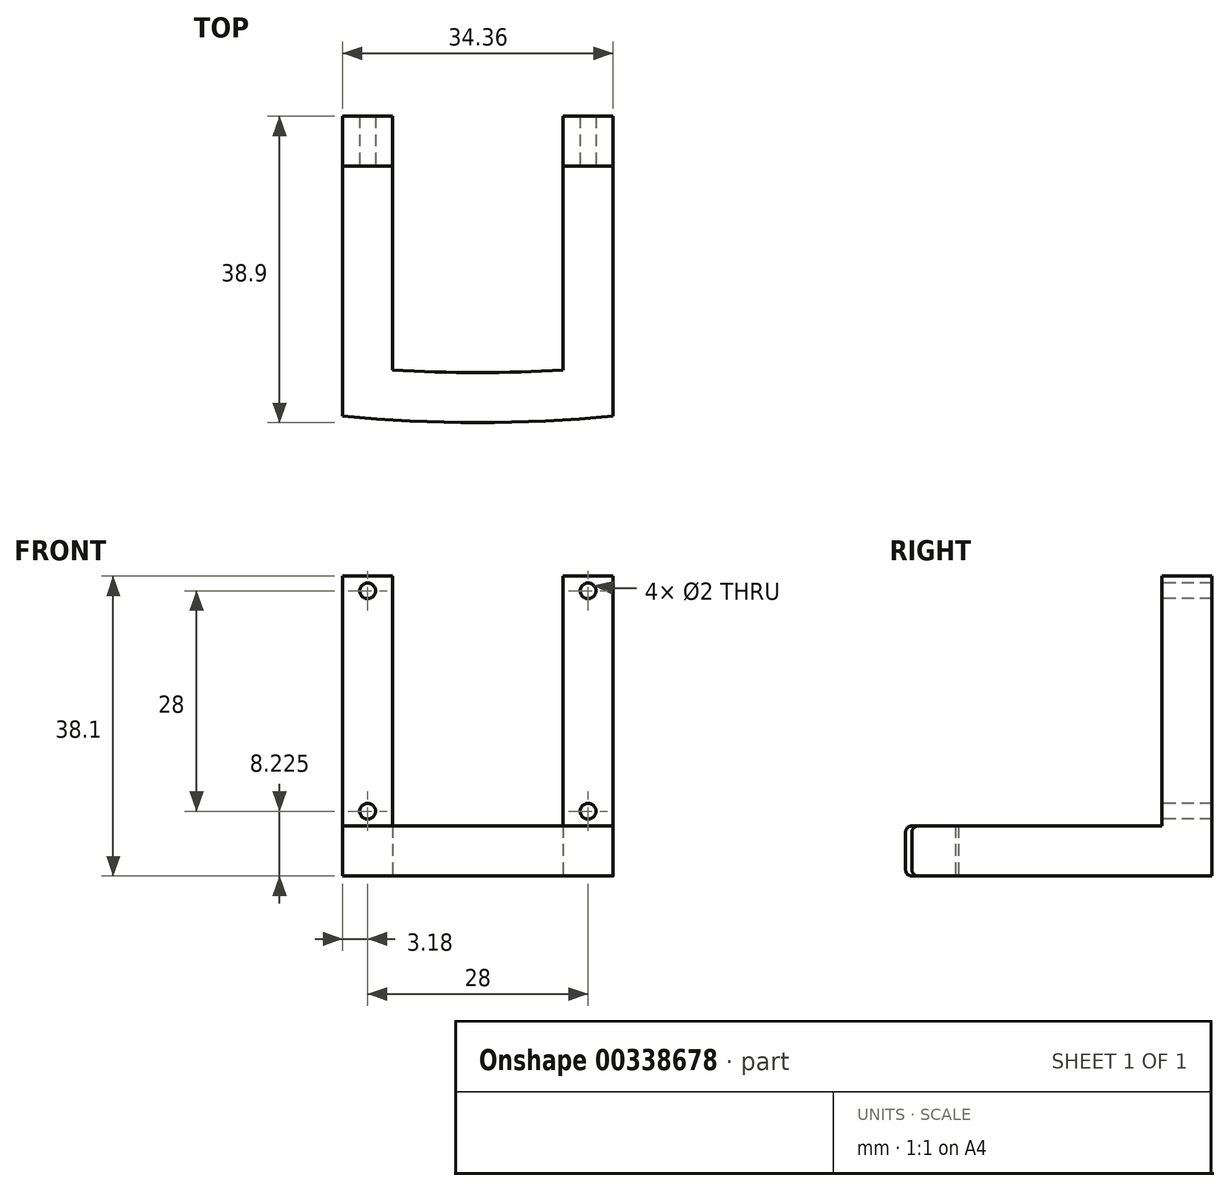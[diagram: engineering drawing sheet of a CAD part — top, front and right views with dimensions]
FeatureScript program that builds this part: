
annotation { "Feature Type Name" : "Feature", "Feature Type Description" : "" }
export const myFeature = defineFeature(function(context is Context, id is Id, definition is map)
    precondition{}
    {
        {
            var Q0;
            Q0=qCreatedBy(makeId("Top.planeOp"),FACE);
            var sketch = newSketch(context, id + "F0", { "sketchPlane" : qUnion([Q0])});
            skLineSegment(sketch, "E0.bottom", {"start": v(-10.82, 0) * mm, "end": v(-17.18, 0) * mm});
            skLineSegment(sketch, "E0.top", {"start": v(-10.82, 38.1) * mm, "end": v(-17.17, 38.1) * mm});
            skLineSegment(sketch, "E0.left", {"start": v(-10.82, 0) * mm, "end": v(-10.82, 38.1) * mm});
            skLineSegment(sketch, "E0.right", {"start": v(-17.18, 0) * mm, "end": v(-17.17, 38.1) * mm});
            skLineSegment(sketch, "E1.bottom", {"start": v(10.82, 0) * mm, "end": v(17.18, 0) * mm});
            skLineSegment(sketch, "E1.top", {"start": v(10.82, 38.1) * mm, "end": v(17.17, 38.1) * mm});
            skLineSegment(sketch, "E1.left", {"start": v(10.82, 0) * mm, "end": v(10.82, 38.1) * mm});
            skLineSegment(sketch, "E1.right", {"start": v(17.18, 0) * mm, "end": v(17.17, 38.1) * mm});
            skArc(sketch, "E2", {"start": v(-17.18, 0) * mm, "mid": v(0, -0.8) * mm, "end": v(17.17, 0) * mm});
            skArc(sketch, "E3", {"start": v(-10.83, 5.88) * mm, "mid": v(0, 5.55) * mm, "end": v(10.82, 5.88) * mm});
            skLineSegment(sketch, "E4.bottom", {"start": v(-17.17, 38.1) * mm, "end": v(-10.82, 38.1) * mm});
            skLineSegment(sketch, "E4.top", {"start": v(-17.17, 31.76) * mm, "end": v(-10.82, 31.76) * mm});
            skLineSegment(sketch, "E4.left", {"start": v(-17.17, 38.1) * mm, "end": v(-17.17, 31.76) * mm});
            skLineSegment(sketch, "E4.right", {"start": v(-10.82, 38.1) * mm, "end": v(-10.82, 31.76) * mm});
            skLineSegment(sketch, "E5.MirrorCS", {"start": v(10.82, 38.1) * mm, "end": v(10.82, 31.76) * mm});
            skLineSegment(sketch, "E6.MirrorCS", {"start": v(17.17, 38.1) * mm, "end": v(17.17, 31.76) * mm});
            skLineSegment(sketch, "E7.MirrorCS", {"start": v(17.17, 38.1) * mm, "end": v(10.82, 38.1) * mm});
            skLineSegment(sketch, "E8.MirrorCS", {"start": v(17.17, 31.76) * mm, "end": v(10.82, 31.76) * mm});
            skLineSegment(sketch, "E9", {"start": v(10.82, 31.76) * mm, "end": v(10.82, 5.88) * mm});
            skSolve(sketch);
        }
        {
            var Q0;
            Q0=qCreatedBy(makeId("Top.planeOp"),FACE);
            var sketch = newSketch(context, id + "F1", { "sketchPlane" : qUnion([Q0])});
            skLineSegment(sketch, "E10.bottom", {"start": v(-17.18, 38.1) * mm, "end": v(-10.82, 38.1) * mm});
            skLineSegment(sketch, "E10.top", {"start": v(-17.18, 31.75) * mm, "end": v(-10.82, 31.75) * mm});
            skLineSegment(sketch, "E10.left", {"start": v(-17.18, 38.1) * mm, "end": v(-17.18, 31.75) * mm});
            skLineSegment(sketch, "E10.right", {"start": v(-10.82, 38.1) * mm, "end": v(-10.82, 31.75) * mm});
            skLineSegment(sketch, "E11.bottom", {"start": v(10.82, 38.1) * mm, "end": v(17.18, 38.1) * mm});
            skLineSegment(sketch, "E11.top", {"start": v(10.82, 31.75) * mm, "end": v(17.18, 31.75) * mm});
            skLineSegment(sketch, "E11.left", {"start": v(10.82, 38.1) * mm, "end": v(10.82, 31.75) * mm});
            skLineSegment(sketch, "E11.right", {"start": v(17.18, 38.1) * mm, "end": v(17.18, 31.75) * mm});
            skSolve(sketch);
        }
        {
            var Q0;
            Q0 = qSketchRegion(id + "F0", true);
            extrude(context, id + "F2", {"entities" : qUnion([Q0]), "depth" : 6.35 * mm});
        }
        {
            var Q0;
            Q0 = qSketchRegion(id + "F1", true);
            extrude(context, id + "F3", {"entities" : qUnion([Q0]), "operationType" : NewBodyOperationType.ADD, "depth" : 38.1 * mm});
        }
        {
            var Q0;
            Q0=makeQuery(id+"F3.opExtrude","SWEPT_FACE",FACE,{"disambiguationData":[OSD([sQuery(id+"F1.wireOp",EDGE,"E10.top")])]});
            var sketch = newSketch(context, id + "F4", { "sketchPlane" : qUnion([Q0])});
            skPoint(sketch, "E12", {"position": v(-14, 36.23) * mm});
            skPoint(sketch, "E12.positionSnap0", {"position": v(-14, 38.1) * mm});
            skPoint(sketch, "E13", {"position": v(-14, 8.22) * mm});
            skPoint(sketch, "E14.MirrorP", {"position": v(14, 36.23) * mm});
            skPoint(sketch, "E15.MirrorP", {"position": v(14, 8.22) * mm});
            skSolve(sketch);
        }
        {
            var Q0;
            Q0=sQuery(id+"F4.wireOp",VERTEX,"E12");
            var Q1;
            Q1=sQuery(id+"F4.wireOp",VERTEX,"E13");
            var Q2;
            Q2=sQuery(id+"F4.wireOp",VERTEX,"E15.MirrorP");
            var Q3;
            Q3=sQuery(id+"F4.wireOp",VERTEX,"E14.MirrorP");
            var Q4;
            Q4=makeQuery(id+"F2.opExtrude","SWEPT_BODY",BODY,{"disambiguationData":[OSD([sQuery(id+"F0.wireOp",EDGE,"E0.top"),sQuery(id+"F0.wireOp",EDGE,"E0.left"),sQuery(id+"F0.wireOp",EDGE,"E0.right"),sQuery(id+"F0.wireOp",EDGE,"E1.top"),sQuery(id+"F0.wireOp",EDGE,"E1.left"),sQuery(id+"F0.wireOp",EDGE,"E1.right"),sQuery(id+"F0.wireOp",EDGE,"E2"),sQuery(id+"F0.wireOp",EDGE,"E3")])]});
            hole(context, id + "F5", {"style" : HoleStyle.SIMPLE, "endStyle" : HoleEndStyle.THROUGH, "holeDiameter" : 2 * mm, "tappedDepth" : 12.7 * mm, "tapClearance" : 3, "locations" : qUnion([Q0, Q1, Q2, Q3]), "scope" : qUnion([Q4])});
        }
        {
            var Q0;
            Q0=makeQuery(id+"F2.opExtrude","CAP_EDGE",EDGE,{"disambiguationData":[OSD([sQuery(id+"F0.wireOp",EDGE,"E2")])],"isStart":false});
            var Q1;
            Q1=makeQuery(id+"F2.opExtrude","CAP_EDGE",EDGE,{"disambiguationData":[OSD([sQuery(id+"F0.wireOp",EDGE,"E2")])],"isStart":true});
            fillet(context, id + "F6", {"entities" : qUnion([Q0, Q1]), "radius" : 0.8 * mm, "tangentPropagation" : true, "allowEdgeOverflow" : false});
        }
    });
